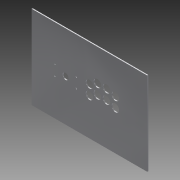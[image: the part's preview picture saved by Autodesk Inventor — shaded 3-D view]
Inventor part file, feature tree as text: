
AUTODESK INVENTOR PART (.ipt)
format: ipt  version: 2013 (Build 170138000, 138)  size: 138,240 bytes
history: native  units: in
note: dims shown in document units (in); Inventor stores cm internally (conversion verified against a paired STEP export)
features: extrude x1, sketch x1
ambient origin geometry x8: Origin, YZ Plane, XZ Plane, XY Plane, X Axis, Y Axis, Z Axis, Center Point
feature tree (2):
  extrude  "Extrusion2"  Depth=13.0in
  sketch  "Sketch1"  dims[d0=18.0in d2=13.0in d3=0.9449in d4=1.1811in d5=3.7402in d6=0.7087in d7=1.1811in d8=0.8268in d9=1.1811in d10=1.1811in d11=1.2303in d12=1.5354in d13=1.1811in d14=1.1811in d15=1.4173in d16=1.5354in d17=1.1811in d18=1.1811in d20=1.378in d21=0.3543in d22=1.1811in d27=3.3465in d28=1.5945in d29=0.1969in d30=0.1969in d31=0.1969in d32=0.1969in d33=1.5945in d34=3.3465in d35=0.1575in d36=0.0in]
